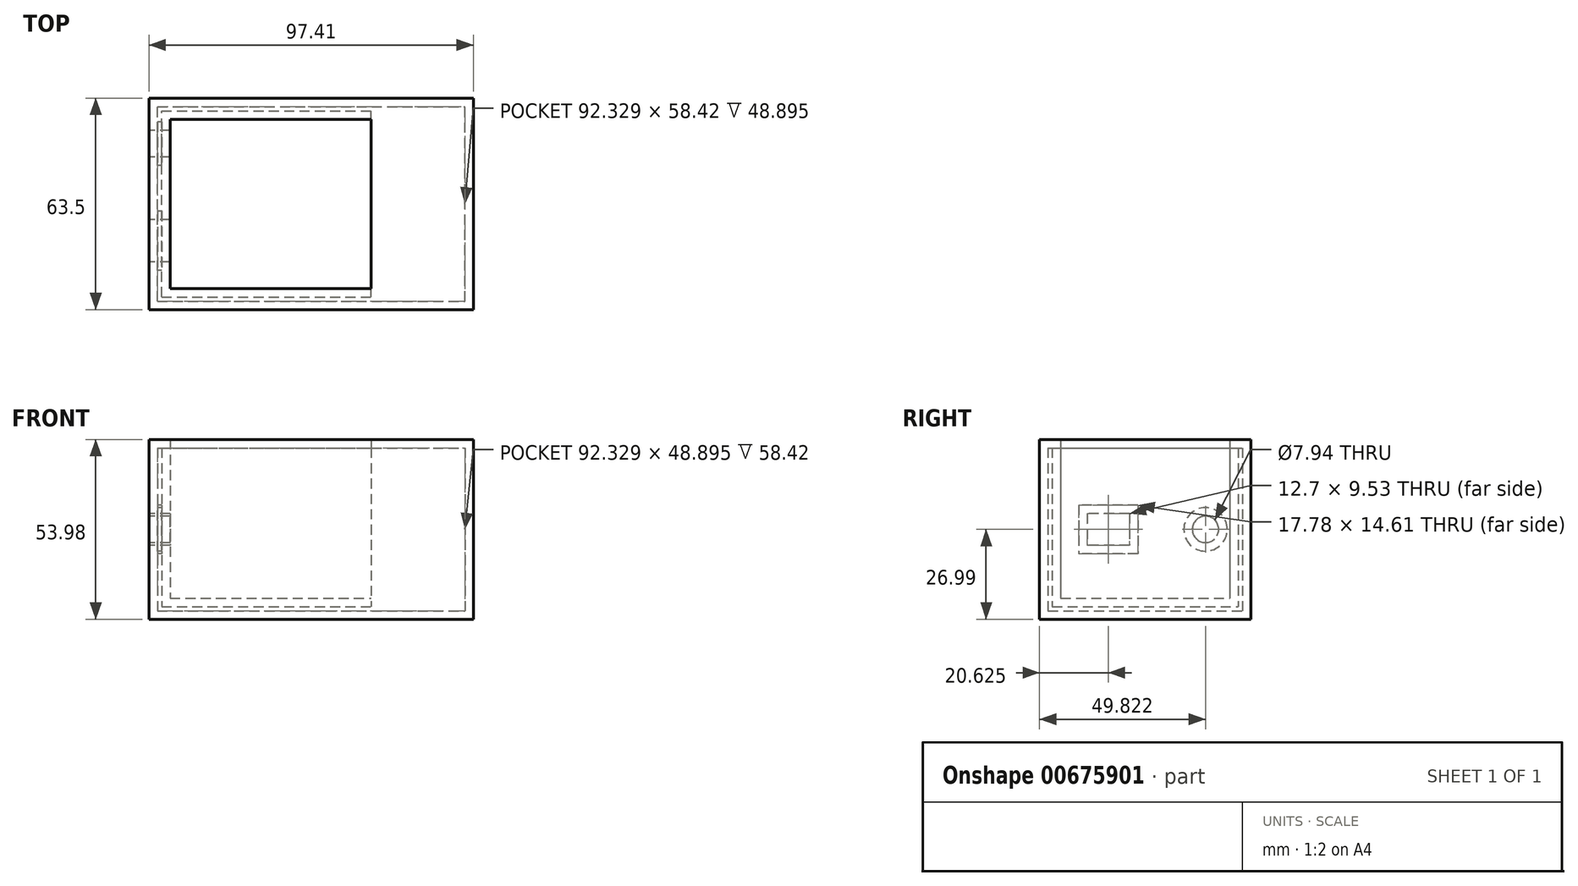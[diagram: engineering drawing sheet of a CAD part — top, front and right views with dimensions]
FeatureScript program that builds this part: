
annotation { "Feature Type Name" : "Feature", "Feature Type Description" : "" }
export const myFeature = defineFeature(function(context is Context, id is Id, definition is map)
    precondition{}
    {
        {
            var Q0;
            Q0=qCreatedBy(makeId("Front.planeOp"),FACE);
            var sketch = newSketch(context, id + "F0", { "sketchPlane" : qUnion([Q0])});
            skLineSegment(sketch, "E0.bottom", {"start": v(-36.51, 26.99) * mm, "end": v(36.51, 26.99) * mm});
            skLineSegment(sketch, "E0.top", {"start": v(-36.51, -26.99) * mm, "end": v(36.51, -26.99) * mm});
            skLineSegment(sketch, "E0.left", {"start": v(-36.51, 26.99) * mm, "end": v(-36.51, -26.99) * mm});
            skLineSegment(sketch, "E0.right", {"start": v(36.51, 26.99) * mm, "end": v(36.51, -26.99) * mm});
            skPoint(sketch, "E0.middle", {"position": v(0, 0) * mm});
            skSolve(sketch);
        }
        {
            var Q0;
            Q0=makeQuery(id+"F0.imprint","IMPRINT",FACE,{"disambiguationData":[TD([[makeQuery(id+"F0.imprint","IMPRINT",EDGE,{"derivedFrom":sQuery(id+"F0.wireOp",EDGE,"E0.bottom")}),-1.0]])]});
            extrude(context, id + "F1", {"entities" : qUnion([Q0]), "depth" : 63.5 * mm, "offsetDistance" : 25.4 * mm});
        }
        {
            var Q0;
            Q0=makeQuery(id+"F1.opExtrude","SWEPT_FACE",FACE,{"disambiguationData":[OSD([sQuery(id+"F0.wireOp",EDGE,"E0.bottom")])]});
            shell(context, id + "F2", {"entities" : qUnion([Q0]), "thickness" : 6.35 * mm});
        }
        {
            var Q0;
            Q0=makeQuery(id+"F1.opExtrude","SWEPT_FACE",FACE,{"disambiguationData":[OSD([sQuery(id+"F0.wireOp",EDGE,"E0.left")])]});
            var sketch = newSketch(context, id + "F3", { "sketchPlane" : qUnion([Q0])});
            skPoint(sketch, "E1", {"position": v(13.68, 0) * mm});
            skPoint(sketch, "E2", {"position": v(42.87, 0) * mm});
            skCircle(sketch, "E3", {"center": v(13.68, 0) * mm, "radius": 3.97 * mm});
            skLineSegment(sketch, "E4.bottom", {"start": v(36.52, 4.76) * mm, "end": v(49.22, 4.76) * mm});
            skLineSegment(sketch, "E4.top", {"start": v(36.52, -4.76) * mm, "end": v(49.22, -4.76) * mm});
            skLineSegment(sketch, "E4.left", {"start": v(36.52, 4.76) * mm, "end": v(36.52, -4.76) * mm});
            skLineSegment(sketch, "E4.right", {"start": v(49.22, 4.76) * mm, "end": v(49.22, -4.76) * mm});
            skSolve(sketch);
        }
        {
            var Q0;
            Q0=makeQuery(id+"F3.imprint","IMPRINT",FACE,{"disambiguationData":[TD([[makeQuery(id+"F3.imprint","IMPRINT",EDGE,{"derivedFrom":sQuery(id+"F3.wireOp",EDGE,"E4.bottom")}),-1.0]])]});
            var sketch = newSketch(context, id + "F4", { "sketchPlane" : qUnion([Q0])});
            skSolve(sketch);
        }
        {
            var Q0;
            Q0=makeQuery(id+"F4.imprint","IMPRINT",FACE,{"disambiguationData":[TD([[makeQuery(id+"F4.imprint","IMPRINT",EDGE,{"derivedFrom":makeQuery(id+"F3.imprint","IMPRINT",EDGE,{"derivedFrom":sQuery(id+"F3.wireOp",EDGE,"E4.bottom")})}),-1.0]])]});
            var Q1;
            Q1=makeQuery(id+"F3.imprint","IMPRINT",FACE,{"disambiguationData":[TD([[makeQuery(id+"F3.imprint","IMPRINT",EDGE,{"derivedFrom":sQuery(id+"F3.wireOp",EDGE,"E3")}),1.0]])]});
            extrude(context, id + "F5", {"entities" : qUnion([Q0, Q1]), "operationType" : NewBodyOperationType.REMOVE, "endBound" : BoundingType.UP_TO_NEXT, "oppositeDirection" : true, "depth" : 25.4 * mm, "offsetDistance" : 25.4 * mm});
        }
        {
            var Q0;
            Q0=makeQuery(id+"F1.opExtrude","CAP_FACE",FACE,{"disambiguationData":[OSD([sQuery(id+"F0.wireOp",EDGE,"E0.bottom"),sQuery(id+"F0.wireOp",EDGE,"E0.top"),sQuery(id+"F0.wireOp",EDGE,"E0.left"),sQuery(id+"F0.wireOp",EDGE,"E0.right")])],"isStart":false});
            var sketch = newSketch(context, id + "F6", { "sketchPlane" : qUnion([Q0])});
            skSolve(sketch);
        }
        {
            var Q0;
            Q0 = qSketchRegion(id + "F6", true);
            var Q1;
            Q1=makeQuery(id+"F6.imprint","IMPRINT",FACE,{"disambiguationData":[TD([[makeQuery(id+"F6.imprint","IMPRINT",EDGE,{"derivedFrom":makeQuery(id+"F1.opExtrude","CAP_EDGE",EDGE,{"disambiguationData":[OSD([sQuery(id+"F0.wireOp",EDGE,"E0.bottom")])],"isStart":false})}),-1.0]])]});
            extrude(context, id + "F7", {"entities" : qUnion([Q0, Q1]), "operationType" : NewBodyOperationType.ADD, "oppositeDirection" : true, "depth" : 0.25 * mm, "offsetDistance" : 25.4 * mm});
        }
        {
            var Q0;
            Q0=makeQuery(id+"F1.opExtrude","SWEPT_FACE",FACE,{"disambiguationData":[OSD([sQuery(id+"F0.wireOp",EDGE,"E0.right")])]});
            var Q1;
            Q1=makeQuery(id+"F2.opShell","OFFSET_FACE",FACE,{"disambiguationData":[OSD([sQuery(id+"F0.wireOp",EDGE,"E0.right")])]});
            extrude(context, id + "F8", {"entities" : qUnion([Q0, Q1]), "operationType" : NewBodyOperationType.ADD, "depth" : 24.38 * mm, "offsetDistance" : 25.4 * mm});
        }
        {
            var Q0;
            Q0=makeQuery(id+"F2.opShell","OFFSET_FACE",FACE,{"disambiguationData":[OSD([sQuery(id+"F0.wireOp",EDGE,"E0.right")])]});
            var sketch = newSketch(context, id + "F9", { "sketchPlane" : qUnion([Q0])});
            skSolve(sketch);
        }
        {
            var Q0;
            Q0 = qSketchRegion(id + "F9", true);
            var Q1;
            {var subQ0=sQuery(id+"F0.wireOp",EDGE,"E0.right");Q1=makeQuery(id+"F9.imprint","IMPRINT",FACE,{"disambiguationData":[TD([[makeQuery(id+"F9.imprint","IMPRINT",EDGE,{"derivedFrom":makeQuery(id+"F2.opShell","OFFSET_EDGE",EDGE,{"disambiguationData":[OSD([subQ0]),TDD([makeQuery(id+"F1.opExtrude","CAP_EDGE",EDGE,{"disambiguationData":[OSD([subQ0])],"isStart":true})])]})}),1.0]])]});}
            extrude(context, id + "F10", {"entities" : qUnion([Q0, Q1]), "operationType" : NewBodyOperationType.ADD, "oppositeDirection" : true, "depth" : 23.62 * mm, "offsetDistance" : 25.4 * mm});
        }
        {
            var Q0;
            Q0=makeQuery(id+"F2.opShell","OFFSET_FACE",FACE,{"disambiguationData":[OSD([sQuery(id+"F0.wireOp",EDGE,"E0.right")])]});
            shell(context, id + "F11", {"entities" : qUnion([Q0]), "thickness" : 2.54 * mm});
        }
    });
